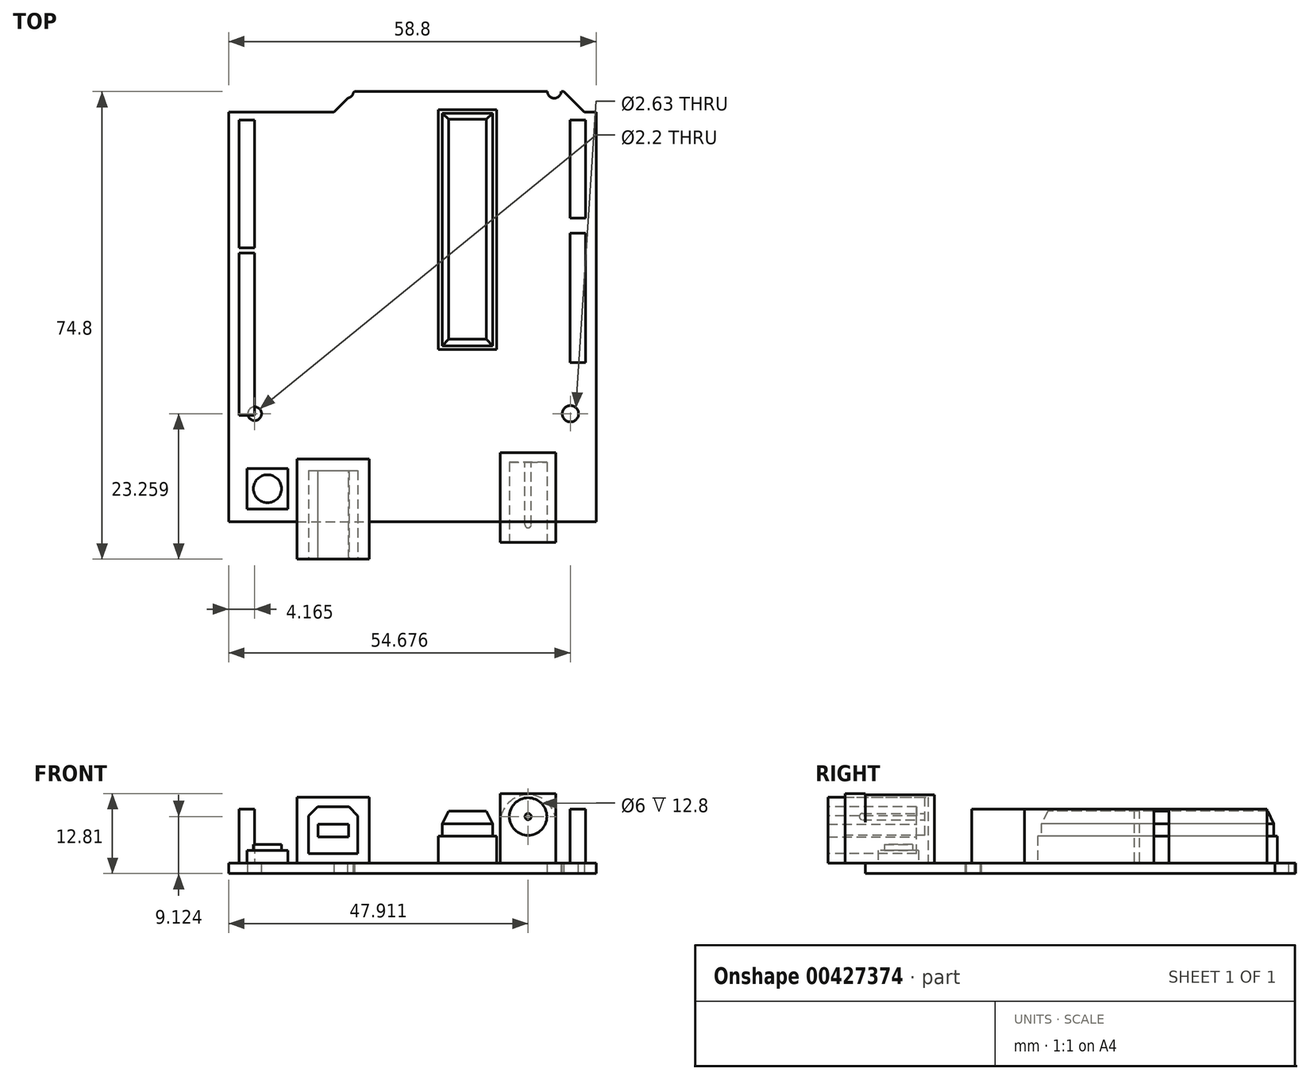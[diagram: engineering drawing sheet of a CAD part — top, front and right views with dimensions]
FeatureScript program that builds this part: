
annotation { "Feature Type Name" : "Feature", "Feature Type Description" : "" }
export const myFeature = defineFeature(function(context is Context, id is Id, definition is map)
    precondition{}
    {
        {
            var Q0;
            Q0=qCreatedBy(makeId("Top.planeOp"),FACE);
            var sketch = newSketch(context, id + "F0", { "sketchPlane" : qUnion([Q0])});
            skLineSegment(sketch, "E0.rect.bottom", {"start": v(-9.27, 34.4) * mm, "end": v(24.2, 34.4) * mm});
            skLineSegment(sketch, "E0.rect.top", {"start": v(-29.4, -34.4) * mm, "end": v(29.4, -34.4) * mm});
            skLineSegment(sketch, "E0.rect.left", {"start": v(-29.4, 31.1) * mm, "end": v(-29.4, -34.4) * mm});
            skLineSegment(sketch, "E0.rect.right", {"start": v(29.4, 31.1) * mm, "end": v(29.4, -34.4) * mm});
            skPoint(sketch, "E0.rect.middle", {"position": v(0, 0) * mm});
            skLineSegment(sketch, "E1.top", {"start": v(-29.4, 31.1) * mm, "end": v(-12.57, 31.1) * mm});
            skPoint(sketch, "E2.orphan", {"position": v(-29.4, 34.4) * mm});
            skLineSegment(sketch, "E3", {"start": v(-9.27, 34.4) * mm, "end": v(-12.57, 31.1) * mm});
            skLineSegment(sketch, "E4.top", {"start": v(27.5, 31.1) * mm, "end": v(29.4, 31.1) * mm});
            skLineSegment(sketch, "E5", {"start": v(24.2, 34.4) * mm, "end": v(27.5, 31.1) * mm});
            skPoint(sketch, "E6.orphan", {"position": v(29.4, 34.4) * mm});
            skSolve(sketch);
        }
        {
            var Q0;
            Q0 = qSketchRegion(id + "F0", true);
            extrude(context, id + "F1", {"entities" : qUnion([Q0]), "depth" : 1.69 * mm, "offsetDistance" : 25 * mm});
        }
        {
            var Q0;
            Q0=makeQuery(id+"F1.opExtrude","CAP_FACE",FACE,{"disambiguationData":[OSD([sQuery(id+"F0.wireOp",EDGE,"E0.rect.bottom"),sQuery(id+"F0.wireOp",EDGE,"E0.rect.top"),sQuery(id+"F0.wireOp",EDGE,"E0.rect.left"),sQuery(id+"F0.wireOp",EDGE,"E0.rect.right"),sQuery(id+"F0.wireOp",EDGE,"E1.top"),sQuery(id+"F0.wireOp",EDGE,"2aa625bf-9bcc-417a-af27-3584bc8afd30"),sQuery(id+"F0.wireOp",EDGE,"E3"),sQuery(id+"F0.wireOp",EDGE,"E4.top"),sQuery(id+"F0.wireOp",EDGE,"E5"),sQuery(id+"F0.wireOp",EDGE,"1fe514a9-330d-4d98-a0d0-b1c185708e78.filletArc"),sQuery(id+"F0.wireOp",EDGE,"4dfaf893-30a7-4712-82e0-8a651be4706f.filletArc"),sQuery(id+"F0.wireOp",EDGE,"47ac2426-5b52-4271-9dd9-c2e938c880cd.filletArc")])],"isStart":false});
            var sketch = newSketch(context, id + "F2", { "sketchPlane" : qUnion([Q0])});
            skLineSegment(sketch, "E7.top", {"start": v(25.23, -8.94) * mm, "end": v(27.73, -8.94) * mm});
            skLineSegment(sketch, "E7.left", {"start": v(25.23, 29.85) * mm, "end": v(25.23, 14.16) * mm});
            skLineSegment(sketch, "E7.right", {"start": v(27.73, 29.85) * mm, "end": v(27.73, 14.16) * mm});
            skLineSegment(sketch, "E8", {"start": v(25.23, 29.85) * mm, "end": v(27.73, 29.85) * mm});
            skLineSegment(sketch, "E9", {"start": v(25.23, 14.16) * mm, "end": v(27.73, 14.16) * mm});
            skLineSegment(sketch, "E10", {"start": v(25.23, 11.76) * mm, "end": v(27.73, 11.76) * mm});
            skLineSegment(sketch, "E11.trimOffspring", {"start": v(25.23, 11.76) * mm, "end": v(25.23, -8.94) * mm});
            skLineSegment(sketch, "E12.trimOffspring", {"start": v(27.73, 11.76) * mm, "end": v(27.73, -8.94) * mm});
            skLineSegment(sketch, "E13.bottom", {"start": v(-27.73, 29.85) * mm, "end": v(-25.23, 29.85) * mm});
            skLineSegment(sketch, "E13.top", {"start": v(-27.73, -17.43) * mm, "end": v(-25.23, -17.43) * mm});
            skLineSegment(sketch, "E13.left", {"start": v(-27.73, 29.85) * mm, "end": v(-27.73, 9.37) * mm});
            skLineSegment(sketch, "E13.right", {"start": v(-25.23, 29.85) * mm, "end": v(-25.23, 9.37) * mm});
            skLineSegment(sketch, "E14.bottom", {"start": v(-27.73, 9.37) * mm, "end": v(-25.23, 9.37) * mm});
            skLineSegment(sketch, "E14.top", {"start": v(-27.73, 8.57) * mm, "end": v(-25.23, 8.57) * mm});
            skLineSegment(sketch, "E15.trimOffspring", {"start": v(-25.23, 8.57) * mm, "end": v(-25.23, -17.43) * mm});
            skLineSegment(sketch, "E16.trimOffspring", {"start": v(-27.73, 8.57) * mm, "end": v(-27.73, -17.43) * mm});
            skSolve(sketch);
        }
        {
            var Q0;
            Q0=makeQuery(id+"F2.imprint","IMPRINT",FACE,{"disambiguationData":[TD([[makeQuery(id+"F2.imprint","IMPRINT",EDGE,{"derivedFrom":sQuery(id+"F2.wireOp",EDGE,"E7.top")}),1.0]])]});
            var Q1;
            Q1=makeQuery(id+"F2.imprint","IMPRINT",FACE,{"disambiguationData":[TD([[makeQuery(id+"F2.imprint","IMPRINT",EDGE,{"derivedFrom":sQuery(id+"F2.wireOp",EDGE,"E7.left")}),1.0]])]});
            var Q2;
            Q2=makeQuery(id+"F2.imprint","IMPRINT",FACE,{"disambiguationData":[TD([[makeQuery(id+"F2.imprint","IMPRINT",EDGE,{"derivedFrom":sQuery(id+"F2.wireOp",EDGE,"E13.bottom")}),-1.0]])]});
            var Q3;
            Q3=makeQuery(id+"F2.imprint","IMPRINT",FACE,{"disambiguationData":[TD([[makeQuery(id+"F2.imprint","IMPRINT",EDGE,{"derivedFrom":sQuery(id+"F2.wireOp",EDGE,"E13.top")}),1.0]])]});
            var Q4;
            {var subQ0=sQuery(id+"F2.wireOp",EDGE,"E14.bottom");Q4=makeQuery(id+"F2.imprint","IMPRINT",FACE,{"disambiguationData":[TD([[makeQuery(id+"F2.imprint","IMPRINT",EDGE,{"derivedFrom":subQ0}),1.0]])]});}
            extrude(context, id + "F3", {"entities" : qUnion([Q0, Q1, Q2, Q3, Q4]), "depth" : 8.6 * mm, "offsetDistance" : 25 * mm});
        }
        {
            var Q0;
            Q0=makeQuery(id+"F1.opExtrude","SWEPT_FACE",FACE,{"disambiguationData":[OSD([sQuery(id+"F0.wireOp",EDGE,"E0.rect.top")])]});
            cPlane(context, id + "F4", {"entities" : qUnion([Q0]), "cplaneType" : CPlaneType.OFFSET, "offset" : 0 * mm, "width" : 150 * mm, "height" : 150 * mm});
        }
        {
            var Q0;
            Q0=qCreatedBy(id+"F4.planeOp",FACE);
            var sketch = newSketch(context, id + "F5", { "sketchPlane" : qUnion([Q0])});
            skLineSegment(sketch, "E17", {"start": v(30.92, 1.68) * mm, "end": v(22.95, 1.68) * mm, "construction": true});
            skLineSegment(sketch, "E18.bottom", {"start": v(22.95, 1.68) * mm, "end": v(14.07, 1.68) * mm});
            skLineSegment(sketch, "E18.left", {"start": v(22.95, 1.68) * mm, "end": v(22.95, 8.18) * mm});
            skLineSegment(sketch, "E18.right", {"start": v(14.07, 1.68) * mm, "end": v(14.07, 8.18) * mm});
            skArc(sketch, "E19", {"start": v(22.95, 8.18) * mm, "mid": v(18.51, 12.62) * mm, "end": v(14.07, 8.18) * mm});
            skSolve(sketch);
        }
        {
            var Q0;
            Q0=makeQuery(id+"F5.imprint","IMPRINT",FACE,{"disambiguationData":[TD([[makeQuery(id+"F5.imprint","IMPRINT",EDGE,{"derivedFrom":sQuery(id+"F5.wireOp",EDGE,"E18.bottom")}),-1.0]])]});
            extrude(context, id + "F6", {"entities" : qUnion([Q0]), "oppositeDirection" : true, "depth" : 11 * mm});
        }
        {
            var Q0;
            Q0=qCreatedBy(id+"F4.planeOp",FACE);
            var sketch = newSketch(context, id + "F7", { "sketchPlane" : qUnion([Q0])});
            skLineSegment(sketch, "E20.bottom", {"start": v(14.07, 1.69) * mm, "end": v(22.95, 1.69) * mm});
            skLineSegment(sketch, "E20.top", {"start": v(14.07, 12.81) * mm, "end": v(22.95, 12.81) * mm});
            skLineSegment(sketch, "E20.left", {"start": v(14.07, 1.69) * mm, "end": v(14.07, 12.81) * mm});
            skLineSegment(sketch, "E20.right", {"start": v(22.95, 1.69) * mm, "end": v(22.95, 12.81) * mm});
            skSolve(sketch);
        }
        {
            var Q0;
            Q0=makeQuery(id+"F7.imprint","IMPRINT",FACE,{"disambiguationData":[TD([[makeQuery(id+"F7.imprint","IMPRINT",EDGE,{"derivedFrom":sQuery(id+"F7.wireOp",EDGE,"E20.bottom")}),1.0]])]});
            extrude(context, id + "F8", {"entities" : qUnion([Q0]), "operationType" : NewBodyOperationType.ADD, "depth" : 3.3 * mm});
        }
        {
            var Q0;
            Q0=makeQuery(id+"F8.opExtrude","CAP_FACE",FACE,{"disambiguationData":[OSD([sQuery(id+"F7.wireOp",EDGE,"E20.bottom"),sQuery(id+"F7.wireOp",EDGE,"E20.top"),sQuery(id+"F7.wireOp",EDGE,"E20.left"),sQuery(id+"F7.wireOp",EDGE,"E20.right")])],"isStart":false});
            var sketch = newSketch(context, id + "F9", { "sketchPlane" : qUnion([Q0])});
            skCircle(sketch, "E21", {"center": v(18.51, 9.12) * mm, "radius": 3 * mm});
            skSolve(sketch);
        }
        {
            var Q0;
            Q0=makeQuery(id+"F9.imprint","IMPRINT",FACE,{"disambiguationData":[TD([[makeQuery(id+"F9.imprint","IMPRINT",EDGE,{"derivedFrom":sQuery(id+"F9.wireOp",EDGE,"E21")}),1.0]])]});
            var Q1;
            Q1=sQuery(id+"F9.wireOp",EDGE,"E21");
            extrude(context, id + "F10", {"entities" : qUnion([Q0]), "operationType" : NewBodyOperationType.REMOVE, "surfaceEntities" : qUnion([Q1]), "oppositeDirection" : true, "depth" : 12.8 * mm});
        }
        {
            var Q0;
            Q0=makeQuery(id+"F10.boolean.opBoolean","COPY",FACE,{"derivedFrom":makeQuery(id+"F10.opExtrude","CAP_FACE",FACE,{"disambiguationData":[OSD([sQuery(id+"F9.wireOp",EDGE,"E21")])],"isStart":false})});
            var sketch = newSketch(context, id + "F11", { "sketchPlane" : qUnion([Q0])});
            skCircle(sketch, "E22.0", {"center": v(18.51, 9.12) * mm, "radius": 3 * mm});
            skCircle(sketch, "E23", {"center": v(18.51, 9.12) * mm, "radius": 0.5 * mm});
            skSolve(sketch);
        }
        {
            var Q0;
            Q0=makeQuery(id+"F11.imprint","IMPRINT",FACE,{"disambiguationData":[TD([[makeQuery(id+"F11.imprint","IMPRINT",EDGE,{"derivedFrom":sQuery(id+"F11.wireOp",EDGE,"E23")}),1.0]])]});
            var Q1;
            Q1=sQuery(id+"F11.wireOp",EDGE,"E23");
            extrude(context, id + "F12", {"entities" : qUnion([Q0]), "surfaceEntities" : qUnion([Q1]), "depth" : 10 * mm});
        }
        {
            var Q0;
            Q0=makeQuery(id+"F1.opExtrude","CAP_FACE",FACE,{"disambiguationData":[OSD([sQuery(id+"F0.wireOp",EDGE,"E0.rect.bottom"),sQuery(id+"F0.wireOp",EDGE,"E0.rect.top"),sQuery(id+"F0.wireOp",EDGE,"E0.rect.left"),sQuery(id+"F0.wireOp",EDGE,"E0.rect.right"),sQuery(id+"F0.wireOp",EDGE,"E1.top"),sQuery(id+"F0.wireOp",EDGE,"2aa625bf-9bcc-417a-af27-3584bc8afd30"),sQuery(id+"F0.wireOp",EDGE,"E3"),sQuery(id+"F0.wireOp",EDGE,"E4.top"),sQuery(id+"F0.wireOp",EDGE,"E5"),sQuery(id+"F0.wireOp",EDGE,"1fe514a9-330d-4d98-a0d0-b1c185708e78.filletArc"),sQuery(id+"F0.wireOp",EDGE,"4dfaf893-30a7-4712-82e0-8a651be4706f.filletArc"),sQuery(id+"F0.wireOp",EDGE,"47ac2426-5b52-4271-9dd9-c2e938c880cd.filletArc")])],"isStart":false});
            var sketch = newSketch(context, id + "F13", { "sketchPlane" : qUnion([Q0])});
            skLineSegment(sketch, "E24.bottom", {"start": v(-18.48, -34.4) * mm, "end": v(-6.88, -34.4) * mm});
            skLineSegment(sketch, "E24.top", {"start": v(-18.48, -24.4) * mm, "end": v(-6.88, -24.4) * mm});
            skLineSegment(sketch, "E24.left", {"start": v(-18.48, -34.4) * mm, "end": v(-18.48, -24.4) * mm});
            skLineSegment(sketch, "E24.right", {"start": v(-6.88, -34.4) * mm, "end": v(-6.88, -24.4) * mm});
            skSolve(sketch);
        }
        {
            var Q0;
            Q0=makeQuery(id+"F13.imprint","IMPRINT",FACE,{"disambiguationData":[TD([[makeQuery(id+"F13.imprint","IMPRINT",EDGE,{"derivedFrom":sQuery(id+"F13.wireOp",EDGE,"E24.bottom")}),1.0]])]});
            extrude(context, id + "F14", {"entities" : qUnion([Q0]), "depth" : 10.5 * mm});
        }
        {
            var Q0;
            Q0=makeQuery(id+"F14.opExtrude","SWEPT_FACE",FACE,{"disambiguationData":[OSD([sQuery(id+"F13.wireOp",EDGE,"E24.bottom")])]});
            var sketch = newSketch(context, id + "F15", { "sketchPlane" : qUnion([Q0])});
            skLineSegment(sketch, "E25.bottom", {"start": v(-18.48, 12.2) * mm, "end": v(-6.88, 12.2) * mm});
            skLineSegment(sketch, "E25.top", {"start": v(-18.48, 1.69) * mm, "end": v(-6.88, 1.69) * mm});
            skLineSegment(sketch, "E25.left", {"start": v(-18.48, 12.2) * mm, "end": v(-18.48, 1.69) * mm});
            skLineSegment(sketch, "E25.right", {"start": v(-6.88, 12.2) * mm, "end": v(-6.88, 1.69) * mm});
            skSolve(sketch);
        }
        {
            var Q0;
            Q0=makeQuery(id+"F15.imprint","IMPRINT",FACE,{"disambiguationData":[TD([[makeQuery(id+"F15.imprint","IMPRINT",EDGE,{"derivedFrom":sQuery(id+"F15.wireOp",EDGE,"E25.bottom")}),-1.0]])]});
            extrude(context, id + "F16", {"entities" : qUnion([Q0]), "operationType" : NewBodyOperationType.ADD, "depth" : 6 * mm});
        }
        {
            var Q0;
            Q0=makeQuery(id+"F16.opExtrude","CAP_FACE",FACE,{"disambiguationData":[OSD([sQuery(id+"F15.wireOp",EDGE,"E25.bottom"),sQuery(id+"F15.wireOp",EDGE,"E25.top"),sQuery(id+"F15.wireOp",EDGE,"E25.left"),sQuery(id+"F15.wireOp",EDGE,"E25.right")])],"isStart":false});
            var sketch = newSketch(context, id + "F17", { "sketchPlane" : qUnion([Q0])});
            skLineSegment(sketch, "E26.rect.bottom", {"start": v(-16.63, 3.2) * mm, "end": v(-8.73, 3.2) * mm});
            skLineSegment(sketch, "E26.rect.top", {"start": v(-15.19, 10.7) * mm, "end": v(-10.17, 10.7) * mm});
            skLineSegment(sketch, "E26.rect.left", {"start": v(-16.63, 3.2) * mm, "end": v(-16.63, 9.25) * mm});
            skLineSegment(sketch, "E26.rect.right", {"start": v(-8.73, 3.2) * mm, "end": v(-8.73, 9.25) * mm});
            skPoint(sketch, "E26.rect.middle", {"position": v(-12.68, 6.94) * mm});
            skPoint(sketch, "E26.rect.middle.positionSnap0", {"position": v(-18.48, 6.94) * mm});
            skPoint(sketch, "E26.rect.middle.positionSnap1", {"position": v(-12.68, 12.2) * mm});
            skPoint(sketch, "E26.rect.centerSnap0", {"position": v(-18.48, 6.94) * mm});
            skPoint(sketch, "E26.rect.centerSnap1", {"position": v(-12.68, 12.2) * mm});
            skLineSegment(sketch, "E27", {"start": v(-16.63, 9.25) * mm, "end": v(-15.19, 10.7) * mm});
            skLineSegment(sketch, "E28", {"start": v(-10.17, 10.7) * mm, "end": v(-8.73, 9.25) * mm});
            skPoint(sketch, "E29.orphan", {"position": v(-16.63, 10.7) * mm});
            skPoint(sketch, "E30.orphan", {"position": v(-8.73, 10.7) * mm});
            skSolve(sketch);
        }
        {
            var Q0;
            Q0=makeQuery(id+"F17.imprint","IMPRINT",FACE,{"disambiguationData":[TD([[makeQuery(id+"F17.imprint","IMPRINT",EDGE,{"derivedFrom":sQuery(id+"F17.wireOp",EDGE,"E26.rect.bottom")}),1.0]])]});
            extrude(context, id + "F18", {"entities" : qUnion([Q0]), "operationType" : NewBodyOperationType.REMOVE, "oppositeDirection" : true, "depth" : 14.14 * mm});
        }
        {
            var Q0;
            Q0=makeQuery(id+"F18.boolean.opBoolean","COPY",FACE,{"derivedFrom":makeQuery(id+"F18.opExtrude","CAP_FACE",FACE,{"disambiguationData":[OSD([sQuery(id+"F17.wireOp",EDGE,"E26.rect.bottom"),sQuery(id+"F17.wireOp",EDGE,"E26.rect.top"),sQuery(id+"F17.wireOp",EDGE,"E26.rect.left"),sQuery(id+"F17.wireOp",EDGE,"E26.rect.right"),sQuery(id+"F17.wireOp",EDGE,"E27"),sQuery(id+"F17.wireOp",EDGE,"E28")])],"isStart":false})});
            var sketch = newSketch(context, id + "F19", { "sketchPlane" : qUnion([Q0])});
            skLineSegment(sketch, "E31.rect.bottom", {"start": v(-15.12, 5.84) * mm, "end": v(-10.24, 5.84) * mm});
            skLineSegment(sketch, "E31.rect.top", {"start": v(-15.12, 7.92) * mm, "end": v(-10.24, 7.92) * mm});
            skLineSegment(sketch, "E31.rect.left", {"start": v(-15.12, 5.84) * mm, "end": v(-15.12, 7.92) * mm});
            skLineSegment(sketch, "E31.rect.right", {"start": v(-10.24, 5.84) * mm, "end": v(-10.24, 7.92) * mm});
            skPoint(sketch, "E31.rect.middle", {"position": v(-12.68, 6.88) * mm});
            skPoint(sketch, "E31.rect.middle.positionSnap0", {"position": v(-12.68, 10.7) * mm});
            skPoint(sketch, "E31.rect.centerSnap0", {"position": v(-12.68, 10.7) * mm});
            skSolve(sketch);
        }
        {
            var Q0;
            Q0=qSketchRegion(id+"F19",true);
            var Q1;
            Q1=makeQuery(id+"F16.opExtrude","CAP_FACE",FACE,{"disambiguationData":[OSD([sQuery(id+"F15.wireOp",EDGE,"E25.bottom"),sQuery(id+"F15.wireOp",EDGE,"E25.top"),sQuery(id+"F15.wireOp",EDGE,"E25.left"),sQuery(id+"F15.wireOp",EDGE,"E25.right")])],"isStart":false});
            extrude(context, id + "F20", {"entities" : qUnion([Q0]), "endBound" : BoundingType.UP_TO_SURFACE, "endBoundEntityFace" : qUnion([Q1]), "depth" : 25 * mm});
        }
        {
            var Q0;
            Q0=makeQuery(id+"F1.opExtrude","CAP_FACE",FACE,{"disambiguationData":[OSD([sQuery(id+"F0.wireOp",EDGE,"E0.rect.bottom"),sQuery(id+"F0.wireOp",EDGE,"E0.rect.top"),sQuery(id+"F0.wireOp",EDGE,"E0.rect.left"),sQuery(id+"F0.wireOp",EDGE,"E0.rect.right"),sQuery(id+"F0.wireOp",EDGE,"E1.top"),sQuery(id+"F0.wireOp",EDGE,"2aa625bf-9bcc-417a-af27-3584bc8afd30"),sQuery(id+"F0.wireOp",EDGE,"E3"),sQuery(id+"F0.wireOp",EDGE,"E4.top"),sQuery(id+"F0.wireOp",EDGE,"E5"),sQuery(id+"F0.wireOp",EDGE,"1fe514a9-330d-4d98-a0d0-b1c185708e78.filletArc"),sQuery(id+"F0.wireOp",EDGE,"4dfaf893-30a7-4712-82e0-8a651be4706f.filletArc"),sQuery(id+"F0.wireOp",EDGE,"47ac2426-5b52-4271-9dd9-c2e938c880cd.filletArc")])],"isStart":false});
            var sketch = newSketch(context, id + "F21", { "sketchPlane" : qUnion([Q0])});
            skLineSegment(sketch, "E32.rect.bottom", {"start": v(-26.44, -25.9) * mm, "end": v(-19.94, -25.9) * mm});
            skLineSegment(sketch, "E32.rect.top", {"start": v(-26.44, -32.4) * mm, "end": v(-19.94, -32.4) * mm});
            skLineSegment(sketch, "E32.rect.left", {"start": v(-26.44, -25.9) * mm, "end": v(-26.44, -32.4) * mm});
            skLineSegment(sketch, "E32.rect.right", {"start": v(-19.94, -25.9) * mm, "end": v(-19.94, -32.4) * mm});
            skPoint(sketch, "E32.rect.middle", {"position": v(-23.19, -29.14) * mm});
            skSolve(sketch);
        }
        {
            var Q0;
            Q0=makeQuery(id+"F21.imprint","IMPRINT",FACE,{"disambiguationData":[TD([[makeQuery(id+"F21.imprint","IMPRINT",EDGE,{"derivedFrom":sQuery(id+"F21.wireOp",EDGE,"E32.rect.bottom")}),-1.0]])]});
            extrude(context, id + "F22", {"entities" : qUnion([Q0]), "depth" : 2 * mm});
        }
        {
            var Q0;
            Q0=makeQuery(id+"F22.opExtrude","CAP_FACE",FACE,{"disambiguationData":[OSD([sQuery(id+"F21.wireOp",EDGE,"E32.rect.bottom"),sQuery(id+"F21.wireOp",EDGE,"E32.rect.top"),sQuery(id+"F21.wireOp",EDGE,"E32.rect.left"),sQuery(id+"F21.wireOp",EDGE,"E32.rect.right")])],"isStart":false});
            var sketch = newSketch(context, id + "F23", { "sketchPlane" : qUnion([Q0])});
            skCircle(sketch, "E33", {"center": v(-23.19, -29.14) * mm, "radius": 2.24 * mm});
            skPoint(sketch, "E33.centerSnap0", {"position": v(-26.44, -29.14) * mm});
            skSolve(sketch);
        }
        {
            var Q0;
            Q0=makeQuery(id+"F23.imprint","IMPRINT",FACE,{"disambiguationData":[TD([[makeQuery(id+"F23.imprint","IMPRINT",EDGE,{"derivedFrom":sQuery(id+"F23.wireOp",EDGE,"E33")}),1.0]])]});
            extrude(context, id + "F24", {"entities" : qUnion([Q0]), "depth" : 1 * mm});
        }
        {
            var Q0;
            Q0=makeQuery(id+"F1.opExtrude","CAP_FACE",FACE,{"disambiguationData":[OSD([sQuery(id+"F0.wireOp",EDGE,"E0.rect.bottom"),sQuery(id+"F0.wireOp",EDGE,"E0.rect.top"),sQuery(id+"F0.wireOp",EDGE,"E0.rect.left"),sQuery(id+"F0.wireOp",EDGE,"E0.rect.right"),sQuery(id+"F0.wireOp",EDGE,"E1.top"),sQuery(id+"F0.wireOp",EDGE,"2aa625bf-9bcc-417a-af27-3584bc8afd30"),sQuery(id+"F0.wireOp",EDGE,"E3"),sQuery(id+"F0.wireOp",EDGE,"E4.top"),sQuery(id+"F0.wireOp",EDGE,"E5"),sQuery(id+"F0.wireOp",EDGE,"1fe514a9-330d-4d98-a0d0-b1c185708e78.filletArc"),sQuery(id+"F0.wireOp",EDGE,"4dfaf893-30a7-4712-82e0-8a651be4706f.filletArc"),sQuery(id+"F0.wireOp",EDGE,"47ac2426-5b52-4271-9dd9-c2e938c880cd.filletArc")])],"isStart":false});
            var sketch = newSketch(context, id + "F25", { "sketchPlane" : qUnion([Q0])});
            skLineSegment(sketch, "E34.bottom", {"start": v(13.47, 31.5) * mm, "end": v(4.14, 31.5) * mm});
            skLineSegment(sketch, "E34.top", {"start": v(13.47, -6.87) * mm, "end": v(4.14, -6.87) * mm});
            skLineSegment(sketch, "E34.left", {"start": v(13.47, 31.5) * mm, "end": v(13.47, -6.87) * mm});
            skLineSegment(sketch, "E34.right", {"start": v(4.14, 31.5) * mm, "end": v(4.14, -6.87) * mm});
            skSolve(sketch);
        }
        {
            var Q0;
            Q0=makeQuery(id+"F25.imprint","IMPRINT",FACE,{"disambiguationData":[TD([[makeQuery(id+"F25.imprint","IMPRINT",EDGE,{"derivedFrom":sQuery(id+"F25.wireOp",EDGE,"E34.bottom")}),1.0]])]});
            extrude(context, id + "F26", {"entities" : qUnion([Q0]), "depth" : 4.3 * mm});
        }
        {
            var Q0;
            Q0=makeQuery(id+"F26.opExtrude","CAP_FACE",FACE,{"disambiguationData":[OSD([sQuery(id+"F25.wireOp",EDGE,"E34.bottom"),sQuery(id+"F25.wireOp",EDGE,"E34.top"),sQuery(id+"F25.wireOp",EDGE,"E34.left"),sQuery(id+"F25.wireOp",EDGE,"E34.right")])],"isStart":false});
            var sketch = newSketch(context, id + "F27", { "sketchPlane" : qUnion([Q0])});
            skLineSegment(sketch, "E35.rect.bottom", {"start": v(4.76, 30.91) * mm, "end": v(12.84, 30.91) * mm});
            skLineSegment(sketch, "E35.rect.top", {"start": v(4.76, -6.28) * mm, "end": v(12.84, -6.28) * mm});
            skLineSegment(sketch, "E35.rect.left", {"start": v(4.76, 30.91) * mm, "end": v(4.76, -6.28) * mm});
            skLineSegment(sketch, "E35.rect.right", {"start": v(12.84, 30.91) * mm, "end": v(12.84, -6.28) * mm});
            skPoint(sketch, "E35.rect.middle", {"position": v(8.8, 12.32) * mm});
            skPoint(sketch, "E35.rect.middle.positionSnap0", {"position": v(8.8, 31.5) * mm});
            skPoint(sketch, "E35.rect.middle.positionSnap1", {"position": v(4.14, 12.32) * mm});
            skPoint(sketch, "E35.rect.centerSnap0", {"position": v(8.8, 31.5) * mm});
            skPoint(sketch, "E35.rect.centerSnap1", {"position": v(4.14, 12.32) * mm});
            skSolve(sketch);
        }
        {
            var Q0;
            Q0=makeQuery(id+"F27.imprint","IMPRINT",FACE,{"disambiguationData":[TD([[makeQuery(id+"F27.imprint","IMPRINT",EDGE,{"derivedFrom":sQuery(id+"F27.wireOp",EDGE,"E35.rect.bottom")}),-1.0]])]});
            extrude(context, id + "F28", {"entities" : qUnion([Q0]), "depth" : 2 * mm});
        }
        {
            var Q0;
            Q0=makeQuery(id+"F28.opExtrude","CAP_FACE",FACE,{"disambiguationData":[OSD([sQuery(id+"F27.wireOp",EDGE,"E35.rect.bottom"),sQuery(id+"F27.wireOp",EDGE,"E35.rect.top"),sQuery(id+"F27.wireOp",EDGE,"E35.rect.left"),sQuery(id+"F27.wireOp",EDGE,"E35.rect.right")])],"isStart":false});
            cPlane(context, id + "F29", {"entities" : qUnion([Q0]), "cplaneType" : CPlaneType.OFFSET, "offset" : 2 * mm, "width" : 150 * mm, "height" : 150 * mm});
        }
        {
            var Q0;
            Q0=qCreatedBy(id+"F29.planeOp",FACE);
            var sketch = newSketch(context, id + "F30", { "sketchPlane" : qUnion([Q0])});
            skLineSegment(sketch, "E36.bottom", {"start": v(5.78, 29.94) * mm, "end": v(11.83, 29.94) * mm});
            skLineSegment(sketch, "E36.top", {"start": v(5.78, -5.22) * mm, "end": v(11.83, -5.22) * mm});
            skLineSegment(sketch, "E36.left", {"start": v(5.78, 29.94) * mm, "end": v(5.78, -5.22) * mm});
            skLineSegment(sketch, "E36.right", {"start": v(11.83, 29.94) * mm, "end": v(11.83, -5.22) * mm});
            skSolve(sketch);
        }
        {
            var Q1;
            Q1=makeQuery(id+"F30.imprint","IMPRINT",FACE,{"disambiguationData":[TD([[makeQuery(id+"F30.imprint","IMPRINT",EDGE,{"derivedFrom":sQuery(id+"F30.wireOp",EDGE,"E36.bottom")}),-1.0]])]});
            var Q2;
            Q2=makeQuery(id+"F28.opExtrude","CAP_FACE",FACE,{"disambiguationData":[OSD([sQuery(id+"F27.wireOp",EDGE,"E35.rect.bottom"),sQuery(id+"F27.wireOp",EDGE,"E35.rect.top"),sQuery(id+"F27.wireOp",EDGE,"E35.rect.left"),sQuery(id+"F27.wireOp",EDGE,"E35.rect.right")])],"isStart":false});
            loft(context, id + "F31", {"sheetProfilesArray" : [{ "sheetProfileEntities" : qUnion([Q1]) }, { "sheetProfileEntities" : qUnion([Q2]) }]});
        }
        {
            var Q0;
            Q0=makeQuery(id+"F1.opExtrude","CAP_FACE",FACE,{"disambiguationData":[OSD([sQuery(id+"F0.wireOp",EDGE,"E0.rect.bottom"),sQuery(id+"F0.wireOp",EDGE,"E0.rect.top"),sQuery(id+"F0.wireOp",EDGE,"E0.rect.left"),sQuery(id+"F0.wireOp",EDGE,"E0.rect.right"),sQuery(id+"F0.wireOp",EDGE,"E1.top"),sQuery(id+"F0.wireOp",EDGE,"2aa625bf-9bcc-417a-af27-3584bc8afd30"),sQuery(id+"F0.wireOp",EDGE,"E3"),sQuery(id+"F0.wireOp",EDGE,"E4.top"),sQuery(id+"F0.wireOp",EDGE,"E5"),sQuery(id+"F0.wireOp",EDGE,"1fe514a9-330d-4d98-a0d0-b1c185708e78.filletArc"),sQuery(id+"F0.wireOp",EDGE,"4dfaf893-30a7-4712-82e0-8a651be4706f.filletArc"),sQuery(id+"F0.wireOp",EDGE,"47ac2426-5b52-4271-9dd9-c2e938c880cd.filletArc")])],"isStart":false});
            var sketch = newSketch(context, id + "F32", { "sketchPlane" : qUnion([Q0])});
            skCircle(sketch, "E37", {"center": v(-10.52, 34.43) * mm, "radius": 1.1 * mm});
            skCircle(sketch, "E38", {"center": v(22.7, 34.43) * mm, "radius": 1.1 * mm});
            skSolve(sketch);
        }
        {
            var Q0;
            Q0=makeQuery(id+"F32.imprint","IMPRINT",FACE,{"disambiguationData":[TD([[makeQuery(id+"F32.imprint","IMPRINT",EDGE,{"derivedFrom":sQuery(id+"F32.wireOp",EDGE,"E37")}),1.0]])]});
            var Q1;
            Q1=makeQuery(id+"F32.imprint","IMPRINT",FACE,{"disambiguationData":[TD([[makeQuery(id+"F32.imprint","IMPRINT",EDGE,{"derivedFrom":sQuery(id+"F32.wireOp",EDGE,"E38")}),1.0]])]});
            extrude(context, id + "F33", {"entities" : qUnion([Q0, Q1]), "operationType" : NewBodyOperationType.REMOVE, "endBound" : BoundingType.THROUGH_ALL, "oppositeDirection" : true, "depth" : 25 * mm});
        }
        {
            var Q0;
            Q0=makeQuery(id+"F1.opExtrude","CAP_FACE",FACE,{"disambiguationData":[OSD([sQuery(id+"F0.wireOp",EDGE,"E0.rect.bottom"),sQuery(id+"F0.wireOp",EDGE,"E0.rect.top"),sQuery(id+"F0.wireOp",EDGE,"E0.rect.left"),sQuery(id+"F0.wireOp",EDGE,"E0.rect.right"),sQuery(id+"F0.wireOp",EDGE,"E1.top"),sQuery(id+"F0.wireOp",EDGE,"2aa625bf-9bcc-417a-af27-3584bc8afd30"),sQuery(id+"F0.wireOp",EDGE,"E3"),sQuery(id+"F0.wireOp",EDGE,"E4.top"),sQuery(id+"F0.wireOp",EDGE,"E5"),sQuery(id+"F0.wireOp",EDGE,"1fe514a9-330d-4d98-a0d0-b1c185708e78.filletArc"),sQuery(id+"F0.wireOp",EDGE,"4dfaf893-30a7-4712-82e0-8a651be4706f.filletArc"),sQuery(id+"F0.wireOp",EDGE,"47ac2426-5b52-4271-9dd9-c2e938c880cd.filletArc")])],"isStart":false});
            var sketch = newSketch(context, id + "F34", { "sketchPlane" : qUnion([Q0])});
            skCircle(sketch, "E39", {"center": v(-25.23, -17.14) * mm, "radius": 1.1 * mm});
            skCircle(sketch, "E40", {"center": v(25.28, -17.14) * mm, "radius": 1.31 * mm});
            skSolve(sketch);
        }
        {
            var Q0;
            Q0=makeQuery(id+"F34.imprint","IMPRINT",FACE,{"disambiguationData":[TD([[makeQuery(id+"F34.imprint","IMPRINT",EDGE,{"derivedFrom":sQuery(id+"F34.wireOp",EDGE,"E39")}),1.0]])]});
            var Q1;
            Q1=makeQuery(id+"F34.imprint","IMPRINT",FACE,{"disambiguationData":[TD([[makeQuery(id+"F34.imprint","IMPRINT",EDGE,{"derivedFrom":sQuery(id+"F34.wireOp",EDGE,"E40")}),1.0]])]});
            var Q2;
            Q2=sQuery(id+"F34.wireOp",EDGE,"E39");
            var Q3;
            Q3=sQuery(id+"F34.wireOp",EDGE,"E40");
            extrude(context, id + "F35", {"entities" : qUnion([Q0, Q1]), "operationType" : NewBodyOperationType.REMOVE, "surfaceEntities" : qUnion([Q2, Q3]), "endBound" : BoundingType.THROUGH_ALL, "oppositeDirection" : true, "depth" : 25 * mm});
        }
        {
            var Q0;
            Q0=makeQuery(id+"F12.opExtrude","CAP_FACE",FACE,{"disambiguationData":[OSD([sQuery(id+"F11.wireOp",EDGE,"E23")])],"isStart":false});
            var sketch = newSketch(context, id + "F36", { "sketchPlane" : qUnion([Q0])});
            skArc(sketch, "E41.0", {"start": v(18.51, 9.62) * mm, "mid": v(18.01, 9.12) * mm, "end": v(18.51, 8.62) * mm});
            skLineSegment(sketch, "E42", {"start": v(18.51, 9.62) * mm, "end": v(18.51, 8.62) * mm});
            skSolve(sketch);
        }
        {
            var Q0;
            {var subQ2=sQuery(id+"F36.wireOp",EDGE,"E42");Q0=makeQuery(id+"F36.imprint","IMPRINT",FACE,{"disambiguationData":[TD([[makeQuery(id+"F36.imprint","IMPRINT",EDGE,{"derivedFrom":subQ2}),1.0]])]});}
            var Q1;
            Q1=sQuery(id+"F36.wireOp",EDGE,"E42");
            revolve(context, id + "F37", {"operationType" : NewBodyOperationType.ADD, "entities" : qUnion([Q0]), "axis" : qUnion([Q1]), "revolveType" : RevolveType.ONE_DIRECTION, "angle" : 180 * degree});
        }
    });
